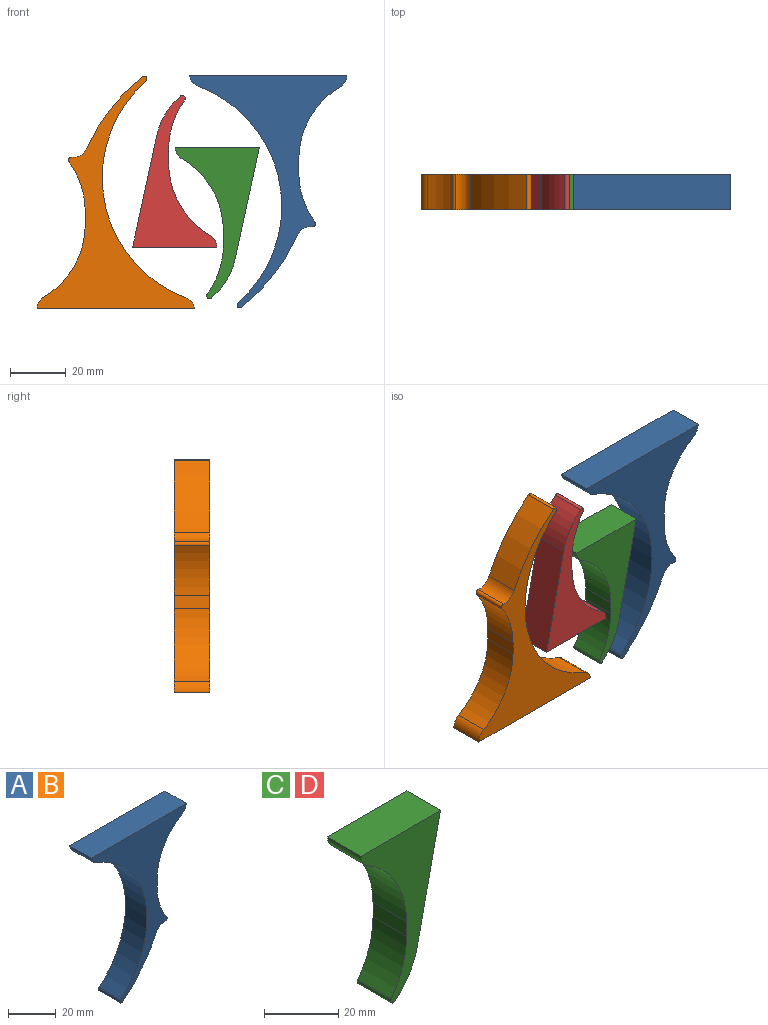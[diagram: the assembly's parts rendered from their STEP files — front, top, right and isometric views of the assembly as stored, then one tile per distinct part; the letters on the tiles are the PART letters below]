
ASSEMBLY  parts=4 mates=3
PART A: 13 faces, bbox 56.5x12.7x83.5 mm
  f0: plane 12.7x4.78mm, normal (1,0,0), area 60.6mm2, adj f1,f10,f11,f12
  f1: cylinder r=30.1mm len=25.94mm, axis (0,1,0), area 397.1mm2, adj f0,f2,f11,f12
  f2: cylinder r=4.95mm len=12.7mm, axis (0,1,0), area 65.2mm2, adj f1,f3,f11,f12
  f3: plane 56.51x12.7mm, normal (0,0,1), area 717.7mm2, adj f2,f4,f11,f12
  f4: cylinder r=4.95mm len=12.7mm, axis (0,1,0), area 68.3mm2, adj f3,f5,f11,f12
  f5: cylinder r=45.97mm len=77.69mm, axis (0,1,0), area 1206.7mm2, adj f4,f6,f11,f12
  f6: cylinder r=1.02mm len=12.7mm, axis (0,1,0), area 39.4mm2, adj f5,f7,f11,f12
  f7: cylinder r=68.58mm len=25.74mm, axis (0,1,0), area 417.9mm2, adj f6,f8,f11,f12
  f8: cylinder r=5.46mm len=12.7mm, axis (0,1,0), area 85.2mm2, adj f7,f9,f11,f12
  f9: cylinder r=1.02mm len=12.7mm, axis (0,1,0), area 29.4mm2, adj f8,f10,f11,f12
  f10: cylinder r=30.1mm len=17.74mm, axis (0,1,0), area 240.9mm2, adj f0,f9,f11,f12
  f11: plane 83.48x56.51mm, normal (0,-1,0), area 1180mm2, adj f0,f1,f2,f3,f4,f5,f6,f7
  f12: plane 83.48x56.51mm, normal (0,1,0), area 1180mm2, adj f0,f1,f2,f3,f4,f5,f6,f7
PART B: same geometry as A
PART C: 10 faces, bbox 30.2x12.7x54.3 mm
  f0: cylinder r=30.1mm len=17.74mm, axis (0,1,0), area 240.9mm2, adj f1,f7,f8,f9
  f1: cylinder r=1.02mm len=12.7mm, axis (0,1,0), area 37.4mm2, adj f0,f2,f8,f9
  f2: cylinder r=25.4mm len=14.12mm, axis (0,1,0), area 213.5mm2, adj f1,f3,f8,f9
  f3: plane 39.97x12.7mm, normal (0.98,0,-0.21), area 519.4mm2, adj f2,f4,f8,f9
  f4: plane 30.16x12.7mm, normal (0,0,1), area 383.1mm2, adj f3,f5,f8,f9
  f5: cylinder r=4.95mm len=12.7mm, axis (0,1,0), area 65.2mm2, adj f4,f6,f8,f9
  f6: cylinder r=30.1mm len=25.94mm, axis (0,1,0), area 397.1mm2, adj f5,f7,f8,f9
  f7: plane 12.7x4.78mm, normal (-1,0,0), area 60.6mm2, adj f0,f6,f8,f9
  f8: plane 54.33x30.16mm, normal (0,-1,0), area 580.7mm2, adj f0,f1,f2,f3,f4,f5,f6,f7
  f9: plane 54.33x30.16mm, normal (0,1,0), area 580.7mm2, adj f0,f1,f2,f3,f4,f5,f6,f7
PART D: same geometry as C
PLACE A t=(-48.09,-13.03,-2.98)mm fixed
PLACE B rot(axis=(0,1,0),180deg) t=(77.53,-13.03,7.37)mm
PLACE C t=(-135.31,-13.03,-28.8)mm
PLACE D rot(axis=(0,1,0),180deg) t=(167.63,-13.03,29.57)mm
MATE planar A.f12 <-> B.f12  axis (0,1,0) through (45.41,-13.03,21.22)mm
MATE planar A.f2 <-> D.f9  axis (0,1,0) through (65.32,-13.03,44.13)mm
MATE planar A.f12 <-> C.f9  axis (0,1,0) through (45.41,-13.03,21.22)mm
